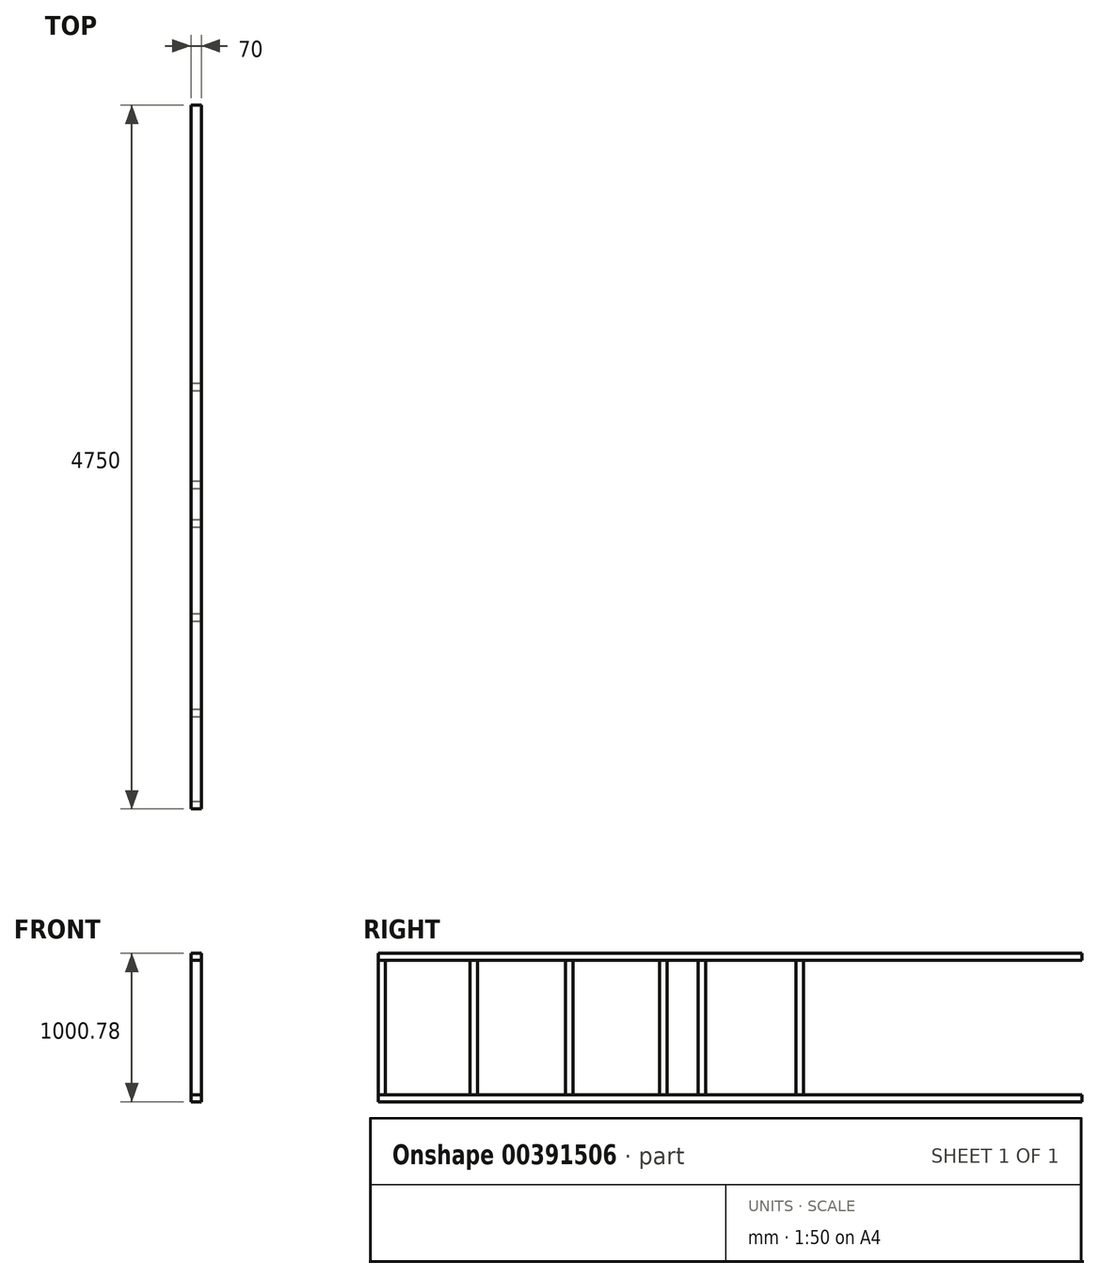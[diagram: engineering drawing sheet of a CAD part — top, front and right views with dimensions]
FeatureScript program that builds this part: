
annotation { "Feature Type Name" : "Feature", "Feature Type Description" : "" }
export const myFeature = defineFeature(function(context is Context, id is Id, definition is map)
    precondition{}
    {
        {
            var Q0;
            Q0=qCreatedBy(makeId("Front.planeOp"),FACE);
            var sketch = newSketch(context, id + "F0", { "sketchPlane" : qUnion([Q0])});
            skLineSegment(sketch, "E0", {"start": v(-1280, 1050) * mm, "end": v(-1280, 0) * mm});
            skLineSegment(sketch, "E1", {"start": v(-1280, 0) * mm, "end": v(0, 0) * mm});
            skLineSegment(sketch, "E2", {"start": v(0, 150) * mm, "end": v(-1280, 1050) * mm});
            skLineSegment(sketch, "E3", {"start": v(0, 150) * mm, "end": v(0, 0) * mm});
            skSolve(sketch);
        }
        {
            var Q0;
            Q0 = qSketchRegion(id + "F0", true);
            var Q1;
            Q1 = qConstructionFilter(qBodyType(qCreatedBy(id + "F0" ,EDGE), BodyType.WIRE), ConstructionObject.NO);
            extrude(context, id + "F1", {"entities" : qUnion([Q0]), "bodyType" : ToolBodyType.SURFACE, "surfaceEntities" : qUnion([Q1]), "endBound" : BoundingType.SYMMETRIC, "depth" : 4750 * mm});
        }
        {
            var Q0;
            Q0=qCreatedBy(makeId("Front.planeOp"),FACE);
            var sketch = newSketch(context, id + "F2", { "sketchPlane" : qUnion([Q0])});
            skLineSegment(sketch, "E4.bottom", {"start": v(-1280, 0) * mm, "end": v(-1210, 0) * mm});
            skLineSegment(sketch, "E4.top", {"start": v(-1280, 45) * mm, "end": v(-1210, 45) * mm});
            skLineSegment(sketch, "E4.left", {"start": v(-1280, 0) * mm, "end": v(-1280, 45) * mm});
            skLineSegment(sketch, "E4.right", {"start": v(-1210, 0) * mm, "end": v(-1210, 45) * mm});
            skLineSegment(sketch, "E5.bottom", {"start": v(-1280, 1000.78) * mm, "end": v(-1210, 1000.78) * mm});
            skLineSegment(sketch, "E5.top", {"start": v(-1280, 955.78) * mm, "end": v(-1210, 955.78) * mm});
            skLineSegment(sketch, "E5.left", {"start": v(-1280, 1000.78) * mm, "end": v(-1280, 955.78) * mm});
            skLineSegment(sketch, "E5.right", {"start": v(-1210, 1000.78) * mm, "end": v(-1210, 955.78) * mm});
            skSolve(sketch);
        }
        {
            var Q0;
            Q0 = qSketchRegion(id + "F2", true);
            extrude(context, id + "F3", {"entities" : qUnion([Q0]), "endBound" : BoundingType.SYMMETRIC, "depth" : 4750 * mm});
        }
        {
            var Q0;
            Q0=makeQuery(id+"F1.opExtrude","SWEPT_FACE",FACE,{"disambiguationData":[OSD([sQuery(id+"F0.wireOp",EDGE,"E0")])]});
            var sketch = newSketch(context, id + "F4", { "sketchPlane" : qUnion([Q0])});
            skLineSegment(sketch, "E6.bottom", {"start": v(2375, 955.78) * mm, "end": v(2325, 955.78) * mm});
            skLineSegment(sketch, "E6.top", {"start": v(2375, 45) * mm, "end": v(2325, 45) * mm});
            skLineSegment(sketch, "E6.left", {"start": v(2375, 955.78) * mm, "end": v(2375, 45) * mm});
            skLineSegment(sketch, "E6.right", {"start": v(2325, 955.78) * mm, "end": v(2325, 45) * mm});
            skLineSegment(sketch, "E7.bottom", {"start": v(1705, 955.78) * mm, "end": v(1755, 955.78) * mm});
            skLineSegment(sketch, "E7.top", {"start": v(1705, 45) * mm, "end": v(1755, 45) * mm});
            skLineSegment(sketch, "E7.left", {"start": v(1705, 955.78) * mm, "end": v(1705, 45) * mm});
            skLineSegment(sketch, "E7.right", {"start": v(1755, 955.78) * mm, "end": v(1755, 45) * mm});
            skLineSegment(sketch, "E8.bottom", {"start": v(1060, 955.78) * mm, "end": v(1110, 955.78) * mm});
            skLineSegment(sketch, "E8.top", {"start": v(1060, 45) * mm, "end": v(1110, 45) * mm});
            skLineSegment(sketch, "E8.left", {"start": v(1060, 955.78) * mm, "end": v(1060, 45) * mm});
            skLineSegment(sketch, "E8.right", {"start": v(1110, 955.78) * mm, "end": v(1110, 45) * mm});
            skLineSegment(sketch, "E9.bottom", {"start": v(425, 955.78) * mm, "end": v(475, 955.78) * mm});
            skLineSegment(sketch, "E9.top", {"start": v(425, 45) * mm, "end": v(475, 45) * mm});
            skLineSegment(sketch, "E9.left", {"start": v(425, 955.78) * mm, "end": v(425, 45) * mm});
            skLineSegment(sketch, "E9.right", {"start": v(475, 955.78) * mm, "end": v(475, 45) * mm});
            skLineSegment(sketch, "E10.bottom", {"start": v(215, 45) * mm, "end": v(165, 45) * mm});
            skLineSegment(sketch, "E10.top", {"start": v(215, 955.78) * mm, "end": v(165, 955.78) * mm});
            skLineSegment(sketch, "E10.left", {"start": v(215, 45) * mm, "end": v(215, 955.78) * mm});
            skLineSegment(sketch, "E10.right", {"start": v(165, 45) * mm, "end": v(165, 955.78) * mm});
            skLineSegment(sketch, "E11.bottom", {"start": v(-445, 45) * mm, "end": v(-495, 45) * mm});
            skLineSegment(sketch, "E11.top", {"start": v(-445, 955.78) * mm, "end": v(-495, 955.78) * mm});
            skLineSegment(sketch, "E11.left", {"start": v(-445, 45) * mm, "end": v(-445, 955.78) * mm});
            skLineSegment(sketch, "E11.right", {"start": v(-495, 45) * mm, "end": v(-495, 955.78) * mm});
            skSolve(sketch);
        }
        {
            var Q0;
            Q0 = qSketchRegion(id + "F4", true);
            var Q1;
            Q1=makeQuery(id+"F3.opExtrude","SWEPT_FACE",FACE,{"disambiguationData":[OSD([sQuery(id+"F2.wireOp",EDGE,"E5.right")])]});
            extrude(context, id + "F5", {"entities" : qUnion([Q0]), "endBound" : BoundingType.UP_TO_SURFACE, "oppositeDirection" : true, "endBoundEntityFace" : qUnion([Q1]), "depth" : 25 * mm});
        }
    });
